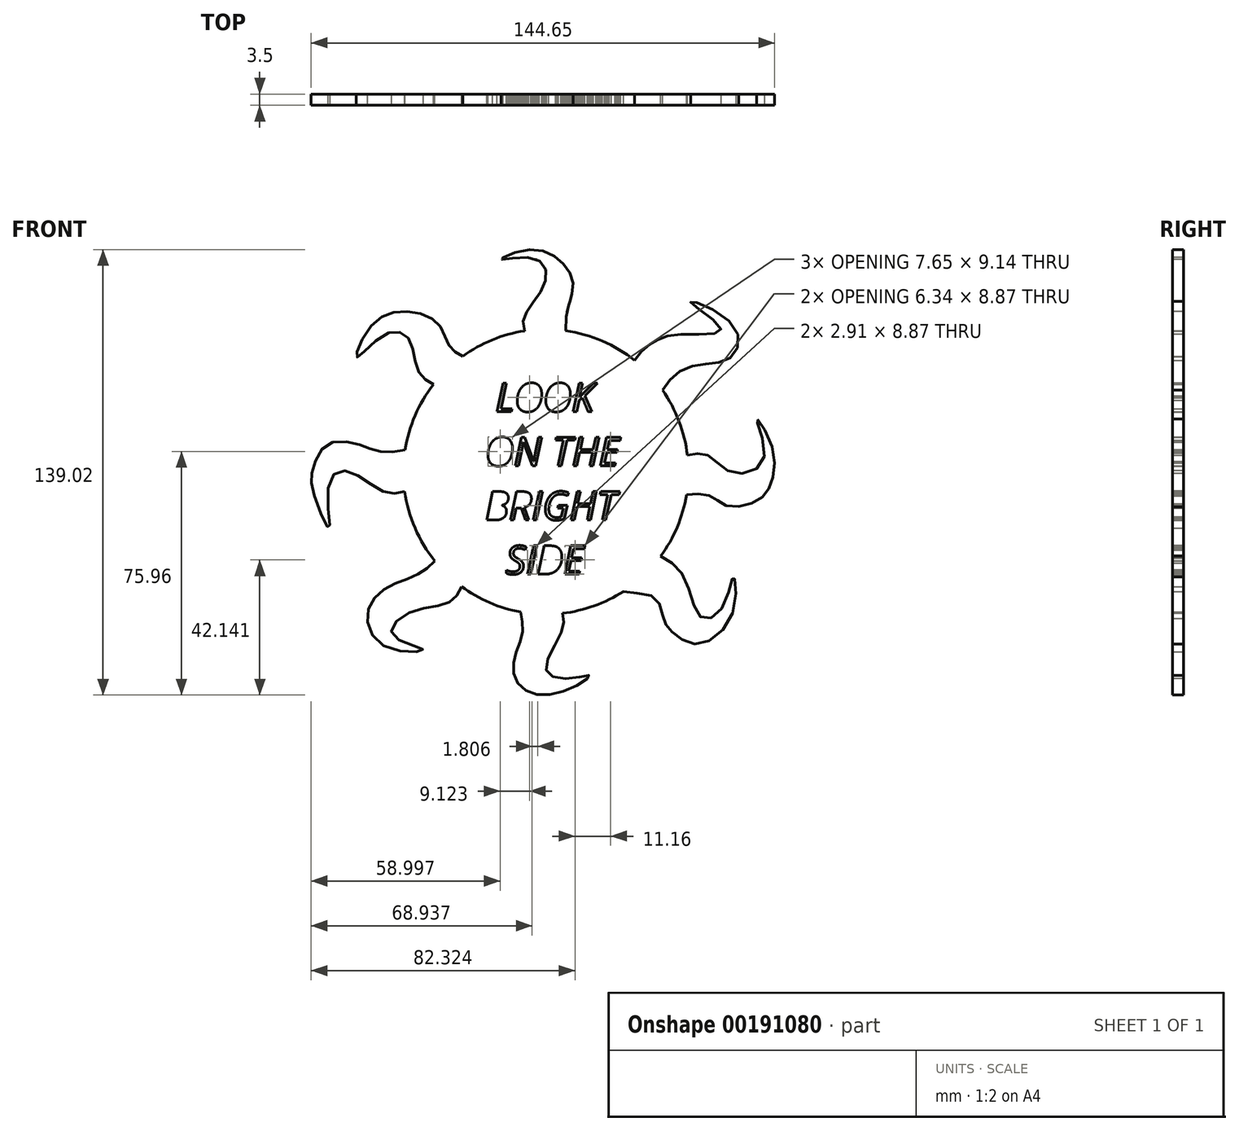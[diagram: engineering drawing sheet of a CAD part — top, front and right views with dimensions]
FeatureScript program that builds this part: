
annotation { "Feature Type Name" : "Feature", "Feature Type Description" : "" }
export const myFeature = defineFeature(function(context is Context, id is Id, definition is map)
    precondition{}
    {
        {
            var Q0;
            Q0=qCreatedBy(makeId("Front.planeOp"),FACE);
            var sketch = newSketch(context, id + "F0", { "sketchPlane" : qUnion([Q0])});
            skCircle(sketch, "E0", {"center": v(0, 0) * mm, "radius": 44.45 * mm});
            skFitSpline(sketch, "E1", {"points": [v(-6.66, 43.95) * mm, v(-5.57, 50.61) * mm, v(0, 60.08) * mm, v(-3.61, 66.64) * mm, v(-13.96, 66.3) * mm, v(-5.65, 69.31) * mm, v(4.94, 65.44) * mm, v(8.51, 57.83) * mm, v(7.36, 52.84) * mm, v(7.35, 52.81) * mm, v(6.17, 44.02) * mm], "startDerivative": vector(-33.45, 77.05) * mm, "endDerivative": vector(15.82, -90.65) * mm});
            skFitSpline(sketch, "E2", {"points": [v(5.19, -44.15) * mm, v(4.9, -49.9) * mm, v(0, -61.4) * mm, v(6.2, -64.58) * mm, v(13.62, -63.6) * mm, v(8.02, -67.48) * mm, v(-3.55, -69.29) * mm, v(-9.6, -64.53) * mm, v(-9.6, -57.42) * mm, v(-7.3, -50.07) * mm, v(-7.9, -43.74) * mm], "startDerivative": vector(11.75, -60.47) * mm, "endDerivative": vector(-15.24, 68.87) * mm});
            skFitSpline(sketch, "E3", {"points": [v(44.15, 5.14) * mm, v(50.3, 5.26) * mm, v(57.72, 0) * mm, v(67.96, 3.83) * mm, v(65.77, 16.4) * mm, v(70.41, 8.36) * mm, v(70.15, -4.05) * mm, v(65.46, -9.29) * mm, v(56.18, -10.52) * mm, v(51.22, -7.43) * mm, v(43.87, -7.17) * mm], "startDerivative": vector(68.04, 19.28) * mm, "endDerivative": vector(-79.2, -8.54) * mm});
            skFitSpline(sketch, "E4", {"points": [v(-44.03, -6.1) * mm, v(-50.6, -6.2) * mm, v(-61.13, 0) * mm, v(-67.63, -3.1) * mm, v(-67.63, -17.64) * mm, v(-72.58, -6.5) * mm, v(-72.9, 0) * mm, v(-68.56, 8.36) * mm, v(-58.96, 8.67) * mm, v(-52.15, 6.5) * mm, v(-43.93, 6.79) * mm], "startDerivative": vector(-71.99, -22.92) * mm, "endDerivative": vector(92.2, 20.69) * mm});
            skFitSpline(sketch, "E5", {"points": [v(-35.12, 27.24) * mm, v(-39.94, 31.63) * mm, v(-42.79, 41.47) * mm, v(-50, 43) * mm, v(-58.98, 35.78) * mm, v(-55.04, 44.98) * mm, v(-44.32, 50) * mm, v(-33.6, 46.29) * mm, v(-30.31, 39.5) * mm, v(-25.95, 36.1) * mm], "startDerivative": vector(-59.84, 31.03) * mm, "endDerivative": vector(59.32, -27.55) * mm});
            skFitSpline(sketch, "E6", {"points": [v(-26.36, -35.79) * mm, v(-30.31, -40.82) * mm, v(-42.57, -43.88) * mm, v(-47.82, -50.89) * mm, v(-38.41, -55.48) * mm, v(-49.57, -54.82) * mm, v(-55.7, -44.32) * mm, v(-50, -36.44) * mm, v(-40.6, -32.28) * mm, v(-34.7, -27.79) * mm], "startDerivative": vector(-32.17, -68.52) * mm, "endDerivative": vector(54.67, 59.97) * mm});
            skFitSpline(sketch, "E7", {"points": [v(35.8, -26.34) * mm, v(43.44, -33.38) * mm, v(48.48, -45.41) * mm, v(55.26, -42.13) * mm, v(58.55, -32.72) * mm, v(58.33, -43.88) * mm, v(47.16, -53.73) * mm, v(39.29, -49.8) * mm, v(36.66, -45.85) * mm, v(34.03, -39.29) * mm, v(24.18, -37.3) * mm], "startDerivative": vector(82.97, -37.19) * mm, "endDerivative": vector(-76.11, 19.7) * mm});
            skFitSpline(sketch, "E8", {"points": [v(27.72, 34.75) * mm, v(33.47, 40.43) * mm, v(41.93, 42.88) * mm, v(54.63, 44.56) * mm, v(45.17, 52.98) * mm, v(58.69, 45.46) * mm, v(57.1, 35.28) * mm, v(45.24, 32.92) * mm, v(36.45, 25.45) * mm], "startDerivative": vector(37.18, 75.65) * mm, "endDerivative": vector(-38.7, -75.8) * mm});
            skPoint(sketch, "E9", {"position": v(52.7, 33.9) * mm});
            skText(sketch, "E10", { "text": " LOOK\nON THE \nBRIGHT \n  SIDE", "fontName": "OpenSans-Italic.ttf"});
            const initialGuessF0  = {"E10": [-0.019, 0.01878, 1, 0, 0.00895]};
            skSetInitialGuess(sketch, initialGuessF0);
            skSolve(sketch);
        }
        {
            var Q0;
            {var subQ0=sQuery(id+"F0.wireOp",EDGE,"E5");Q0=makeQuery(id+"F0.imprint","IMPRINT",FACE,{"disambiguationData":[TD([[makeQuery(id+"F0.imprint","IMPRINT",EDGE,{"derivedFrom":subQ0}),-1.0]])]});}
            var Q1;
            {var subQ0=sQuery(id+"F0.wireOp",EDGE,"E1");Q1=makeQuery(id+"F0.imprint","IMPRINT",FACE,{"disambiguationData":[TD([[makeQuery(id+"F0.imprint","IMPRINT",EDGE,{"derivedFrom":subQ0}),-1.0]])]});}
            var Q2;
            {var subQ0=sQuery(id+"F0.wireOp",EDGE,"E8");Q2=makeQuery(id+"F0.imprint","IMPRINT",FACE,{"disambiguationData":[TD([[makeQuery(id+"F0.imprint","IMPRINT",EDGE,{"derivedFrom":subQ0}),-1.0]])]});}
            var Q3;
            {var subQ0=sQuery(id+"F0.wireOp",EDGE,"E3");Q3=makeQuery(id+"F0.imprint","IMPRINT",FACE,{"disambiguationData":[TD([[makeQuery(id+"F0.imprint","IMPRINT",EDGE,{"derivedFrom":subQ0}),-1.0]])]});}
            var Q4;
            {var subQ0=sQuery(id+"F0.wireOp",EDGE,"E7");Q4=makeQuery(id+"F0.imprint","IMPRINT",FACE,{"disambiguationData":[TD([[makeQuery(id+"F0.imprint","IMPRINT",EDGE,{"derivedFrom":subQ0}),-1.0]])]});}
            var Q5;
            {var subQ0=sQuery(id+"F0.wireOp",EDGE,"E2");Q5=makeQuery(id+"F0.imprint","IMPRINT",FACE,{"disambiguationData":[TD([[makeQuery(id+"F0.imprint","IMPRINT",EDGE,{"derivedFrom":subQ0}),-1.0]])]});}
            var Q6;
            {var subQ0=sQuery(id+"F0.wireOp",EDGE,"E6");Q6=makeQuery(id+"F0.imprint","IMPRINT",FACE,{"disambiguationData":[TD([[makeQuery(id+"F0.imprint","IMPRINT",EDGE,{"derivedFrom":subQ0}),-1.0]])]});}
            var Q7;
            {var subQ0=sQuery(id+"F0.wireOp",EDGE,"E4");Q7=makeQuery(id+"F0.imprint","IMPRINT",FACE,{"disambiguationData":[TD([[makeQuery(id+"F0.imprint","IMPRINT",EDGE,{"derivedFrom":subQ0}),-1.0]])]});}
            var Q8;
            Q8=makeQuery(id+"F0.imprint","IMPRINT",FACE,{"disambiguationData":[TD([[makeQuery(id+"F0.imprint","IMPRINT",EDGE,{"derivedFrom":sQuery(id+"F0.wireOp",EDGE,"E10.sketch_text.stroke-0")}),1.0]])]});
            extrude(context, id + "F1", {"entities" : qUnion([Q0, Q1, Q2, Q3, Q4, Q5, Q6, Q7, Q8]), "depth" : 3.5 * mm});
        }
    });
